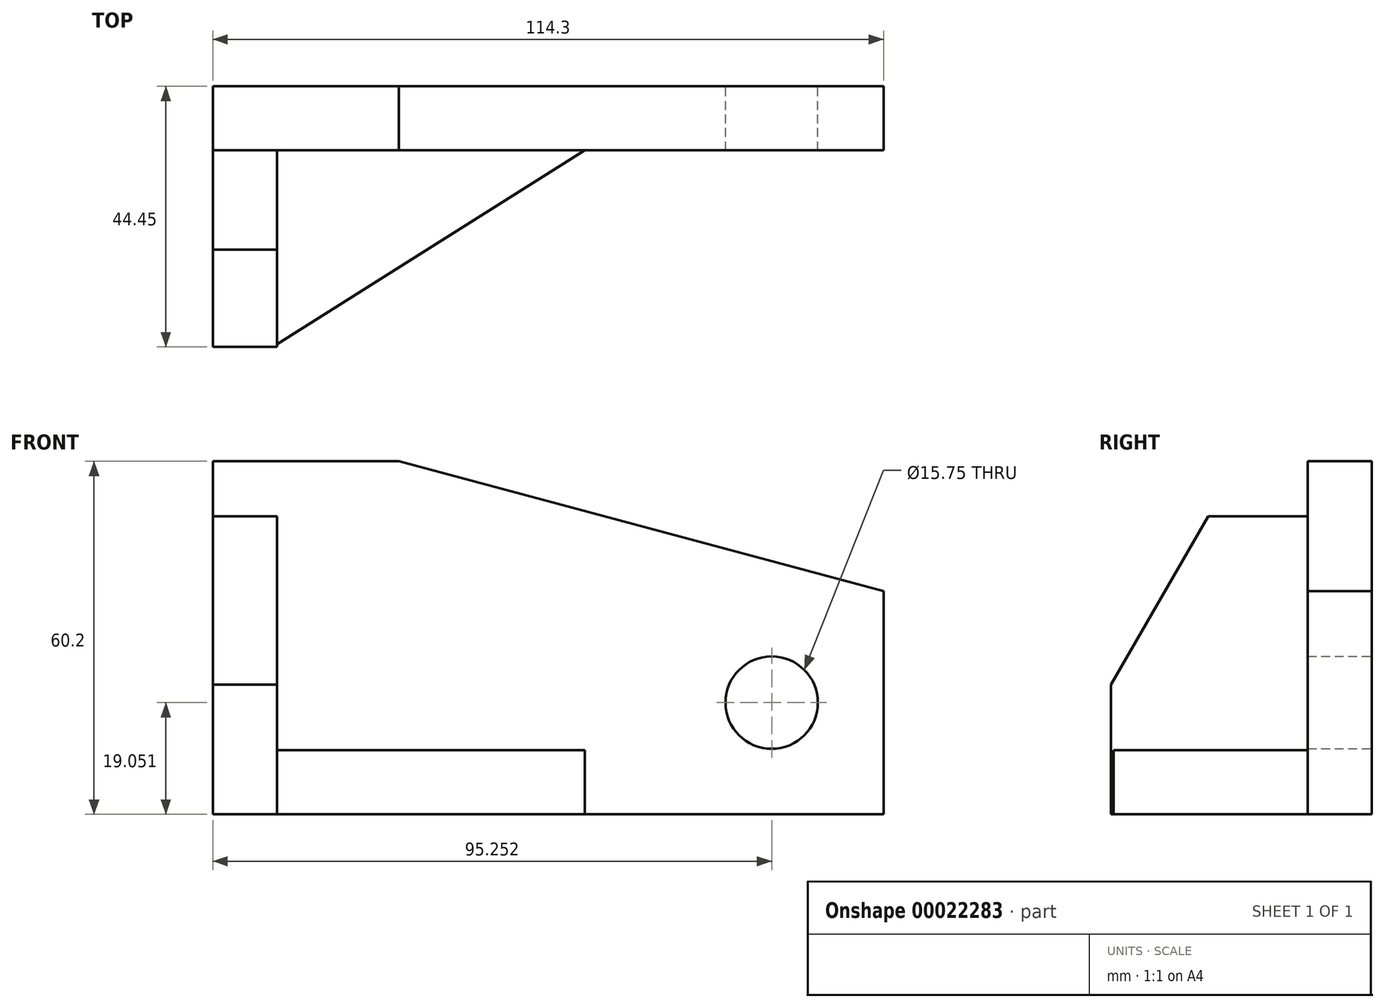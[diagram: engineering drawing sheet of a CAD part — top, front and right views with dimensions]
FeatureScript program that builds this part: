
annotation { "Feature Type Name" : "Feature", "Feature Type Description" : "" }
export const myFeature = defineFeature(function(context is Context, id is Id, definition is map)
    precondition{}
    {
        {
            var Q0;
            Q0=qCreatedBy(makeId("Front.planeOp"),FACE);
            var sketch = newSketch(context, id + "F0", { "sketchPlane" : qUnion([Q0])});
            skLineSegment(sketch, "E0.bottom", {"start": v(-78.03, 22.4) * mm, "end": v(36.27, 22.4) * mm});
            skLineSegment(sketch, "E0.top", {"start": v(-78.03, -37.8) * mm, "end": v(36.27, -37.8) * mm});
            skLineSegment(sketch, "E0.left", {"start": v(-78.03, 22.4) * mm, "end": v(-78.03, -37.8) * mm});
            skLineSegment(sketch, "E0.right", {"start": v(36.27, 22.4) * mm, "end": v(36.27, -37.8) * mm});
            skCircle(sketch, "E1", {"center": v(17.22, -18.75) * mm, "radius": 7.87 * mm});
            skLineSegment(sketch, "E2", {"start": v(-46.28, 22.4) * mm, "end": v(36.27, 0.28) * mm});
            skSolve(sketch);
        }
        {
            var Q0;
            {var subQ2=sQuery(id+"F0.wireOp",EDGE,"E0.top");Q0=makeQuery(id+"F0.imprint","IMPRINT",FACE,{"disambiguationData":[TD([[makeQuery(id+"F0.imprint","IMPRINT",EDGE,{"derivedFrom":subQ2}),1.0]])]});}
            extrude(context, id + "F1", {"entities" : qUnion([Q0]), "depth" : 10.92 * mm});
        }
        {
            var Q0;
            Q0=makeQuery(id+"F1.opExtrude","SWEPT_FACE",FACE,{"disambiguationData":[OSD([sQuery(id+"F0.wireOp",EDGE,"E0.left")])]});
            var sketch = newSketch(context, id + "F2", { "sketchPlane" : qUnion([Q0])});
            skLineSegment(sketch, "E3.bottom", {"start": v(10.92, 13) * mm, "end": v(44.45, 13) * mm});
            skLineSegment(sketch, "E3.top", {"start": v(10.92, -37.8) * mm, "end": v(44.45, -37.8) * mm});
            skLineSegment(sketch, "E3.left", {"start": v(10.92, 13) * mm, "end": v(10.92, -37.8) * mm});
            skLineSegment(sketch, "E3.right", {"start": v(44.45, 13) * mm, "end": v(44.45, -37.8) * mm});
            skLineSegment(sketch, "E4", {"start": v(44.45, -37.8) * mm, "end": v(44.45, -15.7) * mm});
            skLineSegment(sketch, "E5", {"start": v(10.92, 13) * mm, "end": v(27.88, 13) * mm});
            skLineSegment(sketch, "E6", {"start": v(27.88, 13) * mm, "end": v(44.45, -15.7) * mm});
            skSolve(sketch);
        }
        {
            var Q0;
            Q0=makeQuery(id+"F2.imprint","IMPRINT",FACE,{"disambiguationData":[TD([[makeQuery(id+"F2.imprint","IMPRINT",EDGE,{"derivedFrom":sQuery(id+"F2.wireOp",EDGE,"E3.top")}),1.0]])]});
            extrude(context, id + "F3", {"entities" : qUnion([Q0]), "operationType" : NewBodyOperationType.ADD, "oppositeDirection" : true, "depth" : 10.92 * mm});
        }
        {
            var Q0;
            Q0=makeQuery(id+"F1.opExtrude","SWEPT_FACE",FACE,{"disambiguationData":[OSD([sQuery(id+"F0.wireOp",EDGE,"E0.top")])]});
            var sketch = newSketch(context, id + "F4", { "sketchPlane" : qUnion([Q0])});
            skLineSegment(sketch, "E7.bottom", {"start": v(-67.18, 10.92) * mm, "end": v(-14.6, 10.92) * mm});
            skLineSegment(sketch, "E7.top", {"start": v(-67.18, 44.05) * mm, "end": v(-14.6, 44.05) * mm});
            skLineSegment(sketch, "E7.left", {"start": v(-67.18, 10.92) * mm, "end": v(-67.18, 44.05) * mm});
            skLineSegment(sketch, "E7.right", {"start": v(-14.6, 10.92) * mm, "end": v(-14.6, 44.05) * mm});
            skLineSegment(sketch, "E8", {"start": v(-67.18, 44.05) * mm, "end": v(-14.6, 10.92) * mm});
            skSolve(sketch);
        }
        {
            var Q0;
            Q0=makeQuery(id+"F4.imprint","IMPRINT",FACE,{"disambiguationData":[TD([[makeQuery(id+"F4.imprint","IMPRINT",EDGE,{"derivedFrom":sQuery(id+"F4.wireOp",EDGE,"E7.bottom")}),1.0]])]});
            extrude(context, id + "F5", {"entities" : qUnion([Q0]), "operationType" : NewBodyOperationType.ADD, "oppositeDirection" : true, "depth" : 10.92 * mm});
        }
    });
